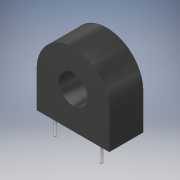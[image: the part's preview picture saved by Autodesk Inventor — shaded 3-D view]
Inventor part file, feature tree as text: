
AUTODESK INVENTOR PART (.ipt)
format: ipt  version: 2018 (Build 220112000, 112)  size: 123,904 bytes
history: native  units: in
note: dims shown in document units (in); Inventor stores cm internally (conversion verified against a paired STEP export)
features: extrude x2, sketch x2
ambient origin geometry x8: Origin, YZ Plane, XZ Plane, XY Plane, X Axis, Y Axis, Z Axis, Center Point
bodies: Solid1 (feature_tree)
feature tree (4):
  extrude  "Extrusion1"  TaperAngle=180.0deg  [1 undecoded]
  extrude  "Extrusion2"  Depth=0.2362in
  sketch  "Sketch1"  dims[d0=0.4685in d1=180.0deg]
  sketch  "Sketch2"  dims[d2=0.4685in d3=0.374in d4=0.937in d5=0.0in d6=0.0689in d7=0.3689in d8=0.0in d9=0.0in d10=0.032in d11=0.032in d12=0.6in d13=0.3in d14=0.032in d15=0.3in d16=0.2362in d17=0.0in]
note: 1 required parameter value undecoded (feature->parameter linkage not recoverable at this tier; creation-order binding heuristic only, values carry confidence <= 0.55)
